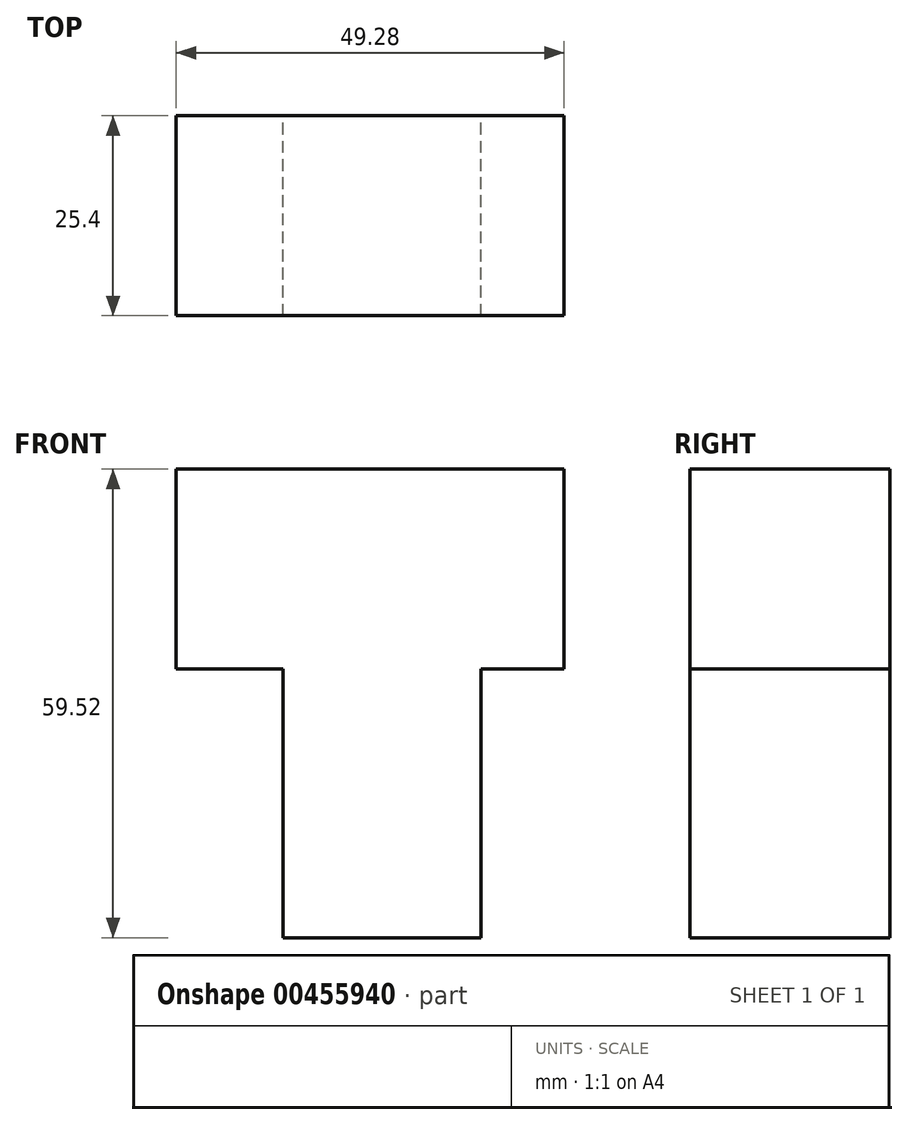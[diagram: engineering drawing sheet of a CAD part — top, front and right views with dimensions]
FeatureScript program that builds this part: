
annotation { "Feature Type Name" : "Feature", "Feature Type Description" : "" }
export const myFeature = defineFeature(function(context is Context, id is Id, definition is map)
    precondition{}
    {
        {
            var Q0;
            Q0=qCreatedBy(makeId("Front.planeOp"),FACE);
            var sketch = newSketch(context, id + "F0", { "sketchPlane" : qUnion([Q0])});
            skLineSegment(sketch, "E0", {"start": v(-13.3, 59.52) * mm, "end": v(-38.7, 59.52) * mm});
            skLineSegment(sketch, "E1", {"start": v(-38.7, 59.52) * mm, "end": v(-38.7, 34.12) * mm});
            skLineSegment(sketch, "E2", {"start": v(-38.7, 34.12) * mm, "end": v(-25.14, 34.12) * mm});
            skLineSegment(sketch, "E3", {"start": v(-25.14, 34.12) * mm, "end": v(-25.14, 0) * mm});
            skLineSegment(sketch, "E4", {"start": v(-25.14, 0) * mm, "end": v(0, 0) * mm});
            skLineSegment(sketch, "E5", {"start": v(0, 0) * mm, "end": v(0, 34.12) * mm});
            skLineSegment(sketch, "E6", {"start": v(0, 34.12) * mm, "end": v(10.57, 34.12) * mm});
            skLineSegment(sketch, "E7", {"start": v(10.57, 34.12) * mm, "end": v(10.57, 59.52) * mm});
            skLineSegment(sketch, "E8", {"start": v(10.57, 59.52) * mm, "end": v(-13.3, 59.52) * mm});
            skSolve(sketch);
        }
        {
            var Q0;
            Q0=makeQuery(id+"F0.imprint","IMPRINT",FACE,{"disambiguationData":[TD([[makeQuery(id+"F0.imprint","IMPRINT",EDGE,{"derivedFrom":sQuery(id+"F0.wireOp",EDGE,"E0")}),1.0]])]});
            extrude(context, id + "F1", {"entities" : qUnion([Q0]), "depth" : 25.4 * mm});
        }
    });
